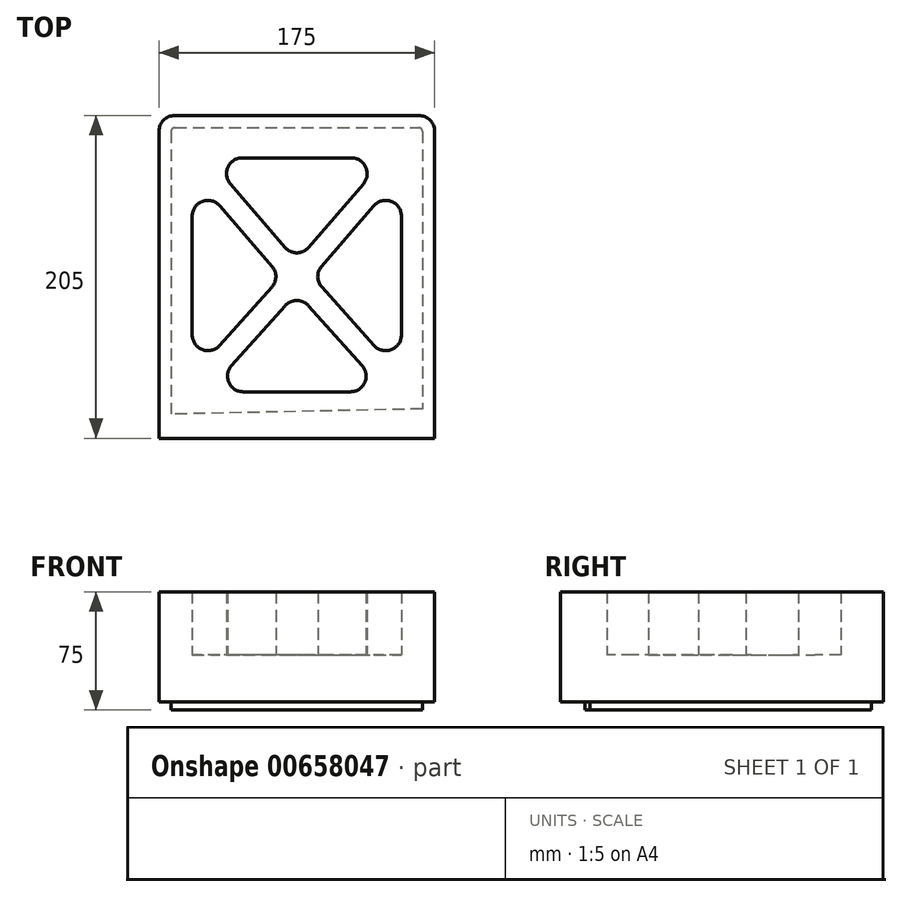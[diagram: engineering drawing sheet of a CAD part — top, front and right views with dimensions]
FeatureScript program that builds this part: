
annotation { "Feature Type Name" : "Feature", "Feature Type Description" : "" }
export const myFeature = defineFeature(function(context is Context, id is Id, definition is map)
    precondition{}
    {
        {
            var Q0;
            Q0=qCreatedBy(makeId("Top.planeOp"),FACE);
            var sketch = newSketch(context, id + "F0", { "sketchPlane" : qUnion([Q0])});
            skLineSegment(sketch, "E0.bottom", {"start": v(-77.5, 102.5) * mm, "end": v(77.5, 102.5) * mm});
            skLineSegment(sketch, "E0.top", {"start": v(-87.5, -102.5) * mm, "end": v(87.5, -102.5) * mm});
            skLineSegment(sketch, "E0.left", {"start": v(-87.5, 92.5) * mm, "end": v(-87.5, -102.5) * mm});
            skLineSegment(sketch, "E0.right", {"start": v(87.5, 92.5) * mm, "end": v(87.5, -102.5) * mm});
            skPoint(sketch, "E0.middle", {"position": v(0, 0) * mm});
            skPoint(sketch, "E1.visualSharp", {"position": v(-87.5, 102.5) * mm});
            skArc(sketch, "E1.filletArc", {"start": v(-77.5, 102.5) * mm, "mid": v(-84.57, 99.57) * mm, "end": v(-87.5, 92.5) * mm});
            skPoint(sketch, "E2.visualSharp", {"position": v(87.5, 102.5) * mm});
            skArc(sketch, "E2.filletArc", {"start": v(87.5, 92.5) * mm, "mid": v(84.57, 99.57) * mm, "end": v(77.5, 102.5) * mm});
            skLineSegment(sketch, "E3.bottom", {"start": v(0, 0) * mm, "end": v(-66.44, 0) * mm});
            skLineSegment(sketch, "E3.top", {"start": v(0, 75.65) * mm, "end": v(-34.65, 75.65) * mm});
            skLineSegment(sketch, "E3.left", {"start": v(0, 0) * mm, "end": v(0, 75.65) * mm});
            skLineSegment(sketch, "E3.right", {"start": v(-66.44, 0) * mm, "end": v(-66.44, 38.68) * mm});
            skLineSegment(sketch, "E4.bottom", {"start": v(-10, 0) * mm, "end": v(-66.44, 0) * mm});
            skLineSegment(sketch, "E4.top", {"start": v(0, -72.94) * mm, "end": v(-34.04, -72.94) * mm});
            skLineSegment(sketch, "E4.left", {"start": v(0, -10) * mm, "end": v(0, -72.94) * mm});
            skLineSegment(sketch, "E4.right", {"start": v(-66.44, 0) * mm, "end": v(-66.44, -36.8) * mm});
            skLineSegment(sketch, "E5.bottom", {"start": v(0, 0) * mm, "end": v(66.44, 0) * mm});
            skLineSegment(sketch, "E5.top", {"start": v(0, 75.65) * mm, "end": v(34.65, 75.65) * mm});
            skLineSegment(sketch, "E5.left", {"start": v(0, 10) * mm, "end": v(0, 75.65) * mm});
            skLineSegment(sketch, "E5.right", {"start": v(66.44, 0) * mm, "end": v(66.44, 38.68) * mm});
            skLineSegment(sketch, "E6.bottom", {"start": v(10, 0) * mm, "end": v(66.44, 0) * mm});
            skLineSegment(sketch, "E6.top", {"start": v(0, -72.94) * mm, "end": v(34.04, -72.94) * mm});
            skLineSegment(sketch, "E6.right", {"start": v(66.44, 0) * mm, "end": v(66.44, -36.8) * mm});
            skLineSegment(sketch, "E7", {"start": v(-15.72, 6.66) * mm, "end": v(-48.85, 45.2) * mm});
            skLineSegment(sketch, "E8", {"start": v(-7.58, 18.82) * mm, "end": v(-42.23, 59.13) * mm});
            skLineSegment(sketch, "E9", {"start": v(7.58, 18.82) * mm, "end": v(42.23, 59.13) * mm});
            skLineSegment(sketch, "E10", {"start": v(15.72, 6.66) * mm, "end": v(48.85, 45.2) * mm});
            skLineSegment(sketch, "E11", {"start": v(-15.86, -6.54) * mm, "end": v(-49, -43.48) * mm});
            skLineSegment(sketch, "E12", {"start": v(-7.45, -18.3) * mm, "end": v(-41.48, -56.26) * mm});
            skLineSegment(sketch, "E13", {"start": v(7.45, -18.3) * mm, "end": v(41.48, -56.26) * mm});
            skLineSegment(sketch, "E14", {"start": v(15.86, -6.54) * mm, "end": v(49, -43.48) * mm});
            skPoint(sketch, "E15.visualSharp", {"position": v(-10, 0) * mm});
            skArc(sketch, "E15.filletArc", {"start": v(-15.86, -6.54) * mm, "mid": v(-13.3, 0.03) * mm, "end": v(-15.72, 6.66) * mm});
            skPoint(sketch, "E16.visualSharp", {"position": v(0, 10) * mm});
            skArc(sketch, "E16.filletArc", {"start": v(-7.58, 18.82) * mm, "mid": v(0, 15.34) * mm, "end": v(7.58, 18.82) * mm});
            skPoint(sketch, "E17.visualSharp", {"position": v(10, 0) * mm});
            skArc(sketch, "E17.filletArc", {"start": v(15.72, 6.66) * mm, "mid": v(13.3, 0.03) * mm, "end": v(15.86, -6.54) * mm});
            skPoint(sketch, "E18.visualSharp", {"position": v(0, -10) * mm});
            skArc(sketch, "E18.filletArc", {"start": v(7.45, -18.3) * mm, "mid": v(0, -14.98) * mm, "end": v(-7.45, -18.3) * mm});
            skArc(sketch, "E19.filletArc", {"start": v(-48.85, 45.2) * mm, "mid": v(-59.91, 48.05) * mm, "end": v(-66.44, 38.68) * mm});
            skArc(sketch, "E20.filletArc", {"start": v(-34.65, 75.65) * mm, "mid": v(-43.74, 69.82) * mm, "end": v(-42.23, 59.13) * mm});
            skArc(sketch, "E21.filletArc", {"start": v(66.44, 38.68) * mm, "mid": v(59.91, 48.05) * mm, "end": v(48.85, 45.2) * mm});
            skArc(sketch, "E22.filletArc", {"start": v(42.23, 59.13) * mm, "mid": v(43.74, 69.82) * mm, "end": v(34.65, 75.65) * mm});
            skArc(sketch, "E23.filletArc", {"start": v(-41.48, -56.26) * mm, "mid": v(-43.17, -67.01) * mm, "end": v(-34.04, -72.94) * mm});
            skArc(sketch, "E24.filletArc", {"start": v(34.04, -72.94) * mm, "mid": v(43.17, -67.01) * mm, "end": v(41.48, -56.26) * mm});
            skArc(sketch, "E25.filletArc", {"start": v(-66.44, -36.8) * mm, "mid": v(-60, -46.15) * mm, "end": v(-49, -43.48) * mm});
            skPoint(sketch, "E26.visualSharp", {"position": v(66.44, -62.94) * mm});
            skArc(sketch, "E26.filletArc", {"start": v(49, -43.48) * mm, "mid": v(60, -46.15) * mm, "end": v(66.44, -36.8) * mm});
            skSolve(sketch);
        }
        {
            var Q0;
            Q0=makeQuery(id+"F0.imprint","IMPRINT",FACE,{"disambiguationData":[TD([[makeQuery(id+"F0.imprint","IMPRINT",EDGE,{"derivedFrom":sQuery(id+"F0.wireOp",EDGE,"E0.bottom")}),-1.0]])]});
            extrude(context, id + "F1", {"entities" : qUnion([Q0]), "depth" : 40 * mm, "offsetDistance" : 25 * mm});
        }
        {
            var Q0;
            Q0 = qSketchRegion(id + "F0", true);
            var Q1;
            Q1=makeQuery(id+"F1.opExtrude","CAP_FACE",FACE,{"disambiguationData":[OSD([sQuery(id+"F0.wireOp",EDGE,"E0.bottom"),sQuery(id+"F0.wireOp",EDGE,"E0.top"),sQuery(id+"F0.wireOp",EDGE,"E0.left"),sQuery(id+"F0.wireOp",EDGE,"E0.right"),sQuery(id+"F0.wireOp",EDGE,"E1.filletArc"),sQuery(id+"F0.wireOp",EDGE,"E2.filletArc")])],"isStart":false});
            var Q2;
            {var subQ1=sQuery(id+"F0.wireOp",EDGE,"E3.right");Q2=makeQuery(id+"F0.imprint","IMPRINT",FACE,{"disambiguationData":[TD([[makeQuery(id+"F0.imprint","IMPRINT",EDGE,{"derivedFrom":subQ1}),-1.0]])]});}
            var Q3;
            {var subQ4=sQuery(id+"F0.wireOp",EDGE,"E3.top");Q3=makeQuery(id+"F0.imprint","IMPRINT",FACE,{"disambiguationData":[TD([[makeQuery(id+"F0.imprint","IMPRINT",EDGE,{"derivedFrom":subQ4}),1.0]])]});}
            var Q4;
            {var subQ4=sQuery(id+"F0.wireOp",EDGE,"E5.top");Q4=makeQuery(id+"F0.imprint","IMPRINT",FACE,{"disambiguationData":[TD([[makeQuery(id+"F0.imprint","IMPRINT",EDGE,{"derivedFrom":subQ4}),-1.0]])]});}
            var Q5;
            {var subQ4=sQuery(id+"F0.wireOp",EDGE,"E5.right");Q5=makeQuery(id+"F0.imprint","IMPRINT",FACE,{"disambiguationData":[TD([[makeQuery(id+"F0.imprint","IMPRINT",EDGE,{"derivedFrom":subQ4}),1.0]])]});}
            var Q6;
            {var subQ4=sQuery(id+"F0.wireOp",EDGE,"E6.right");Q6=makeQuery(id+"F0.imprint","IMPRINT",FACE,{"disambiguationData":[TD([[makeQuery(id+"F0.imprint","IMPRINT",EDGE,{"derivedFrom":subQ4}),-1.0]])]});}
            var Q7;
            {var subQ4=sQuery(id+"F0.wireOp",EDGE,"E6.top");Q7=makeQuery(id+"F0.imprint","IMPRINT",FACE,{"disambiguationData":[TD([[makeQuery(id+"F0.imprint","IMPRINT",EDGE,{"derivedFrom":subQ4}),1.0]])]});}
            var Q8;
            {var subQ4=sQuery(id+"F0.wireOp",EDGE,"E4.top");Q8=makeQuery(id+"F0.imprint","IMPRINT",FACE,{"disambiguationData":[TD([[makeQuery(id+"F0.imprint","IMPRINT",EDGE,{"derivedFrom":subQ4}),-1.0]])]});}
            var Q9;
            {var subQ4=sQuery(id+"F0.wireOp",EDGE,"E4.right");Q9=makeQuery(id+"F0.imprint","IMPRINT",FACE,{"disambiguationData":[TD([[makeQuery(id+"F0.imprint","IMPRINT",EDGE,{"derivedFrom":subQ4}),1.0]])]});}
            extrude(context, id + "F2", {"entities" : qUnion([Q0, Q1, Q2, Q3, Q4, Q5, Q6, Q7, Q8, Q9]), "operationType" : NewBodyOperationType.ADD, "depth" : 30 * mm, "offsetDistance" : 25 * mm});
        }
        {
            var Q0;
            {var subQ0=sQuery(id+"F0.wireOp",EDGE,"E2.filletArc");var subQ1=sQuery(id+"F0.wireOp",EDGE,"E1.filletArc");var subQ2=sQuery(id+"F0.wireOp",EDGE,"E0.right");var subQ3=sQuery(id+"F0.wireOp",EDGE,"E0.left");var subQ4=sQuery(id+"F0.wireOp",EDGE,"E0.top");var subQ5=sQuery(id+"F0.wireOp",EDGE,"E0.bottom");Q0=makeQuery(id+"F2.boolean.opBoolean","MERGE",FACE,{"derivedFrom":[makeQuery(id+"F1.opExtrude","CAP_FACE",FACE,{"disambiguationData":[OSD([subQ5,subQ4,subQ3,subQ2,subQ1,subQ0,sQuery(id+"F0.wireOp",EDGE,"E3.top"),sQuery(id+"F0.wireOp",EDGE,"E3.right"),sQuery(id+"F0.wireOp",EDGE,"E4.top"),sQuery(id+"F0.wireOp",EDGE,"E4.right"),sQuery(id+"F0.wireOp",EDGE,"E5.top"),sQuery(id+"F0.wireOp",EDGE,"E5.right"),sQuery(id+"F0.wireOp",EDGE,"E6.top"),sQuery(id+"F0.wireOp",EDGE,"E6.right"),sQuery(id+"F0.wireOp",EDGE,"E7"),sQuery(id+"F0.wireOp",EDGE,"E8"),sQuery(id+"F0.wireOp",EDGE,"E9"),sQuery(id+"F0.wireOp",EDGE,"E10"),sQuery(id+"F0.wireOp",EDGE,"E11"),sQuery(id+"F0.wireOp",EDGE,"E12"),sQuery(id+"F0.wireOp",EDGE,"E13"),sQuery(id+"F0.wireOp",EDGE,"E14"),sQuery(id+"F0.wireOp",EDGE,"E15.filletArc"),sQuery(id+"F0.wireOp",EDGE,"E16.filletArc"),sQuery(id+"F0.wireOp",EDGE,"E17.filletArc"),sQuery(id+"F0.wireOp",EDGE,"E18.filletArc"),sQuery(id+"F0.wireOp",EDGE,"E19.filletArc"),sQuery(id+"F0.wireOp",EDGE,"E20.filletArc"),sQuery(id+"F0.wireOp",EDGE,"E21.filletArc"),sQuery(id+"F0.wireOp",EDGE,"E22.filletArc"),sQuery(id+"F0.wireOp",EDGE,"E23.filletArc"),sQuery(id+"F0.wireOp",EDGE,"E24.filletArc"),sQuery(id+"F0.wireOp",EDGE,"E25.filletArc"),sQuery(id+"F0.wireOp",EDGE,"E26.filletArc")])],"isStart":true}),makeQuery(id+"F2.opExtrude","CAP_FACE",FACE,{"disambiguationData":[OSD([subQ5,subQ4,subQ3,subQ2,subQ1,subQ0])],"isStart":true})]});}
            var sketch = newSketch(context, id + "F3", { "sketchPlane" : qUnion([Q0])});
            skArc(sketch, "E27.0", {"start": v(-77.5, -94.8) * mm, "mid": v(-79.13, -94.13) * mm, "end": v(-79.8, -92.5) * mm});
            skLineSegment(sketch, "E27.1", {"start": v(-79.8, 94.8) * mm, "end": v(79.8, 94.8) * mm});
            skLineSegment(sketch, "E27.2", {"start": v(79.8, -92.5) * mm, "end": v(79.8, 94.8) * mm});
            skLineSegment(sketch, "E27.3", {"start": v(-79.8, -92.5) * mm, "end": v(-79.8, 94.8) * mm});
            skArc(sketch, "E27.4", {"start": v(79.8, -92.5) * mm, "mid": v(79.13, -94.13) * mm, "end": v(77.5, -94.8) * mm});
            skLineSegment(sketch, "E27.5", {"start": v(-77.5, -94.8) * mm, "end": v(77.5, -94.8) * mm});
            skLineSegment(sketch, "E28", {"start": v(-79.8, 94.8) * mm, "end": v(-79.8, 102.5) * mm});
            skLineSegment(sketch, "E29", {"start": v(79.8, 94.8) * mm, "end": v(79.8, 102.5) * mm});
            skLineSegment(sketch, "E30", {"start": v(79.8, 83.83) * mm, "end": v(-79.8, 87.09) * mm});
            skSolve(sketch);
        }
        {
            var Q0;
            Q0=makeQuery(id+"F3.imprint","IMPRINT",FACE,{"disambiguationData":[TD([[makeQuery(id+"F3.imprint","IMPRINT",EDGE,{"derivedFrom":sQuery(id+"F3.wireOp",EDGE,"E27.0")}),1.0]])]});
            extrude(context, id + "F4", {"entities" : qUnion([Q0]), "operationType" : NewBodyOperationType.ADD, "depth" : 5 * mm, "offsetDistance" : 25 * mm});
        }
    });
